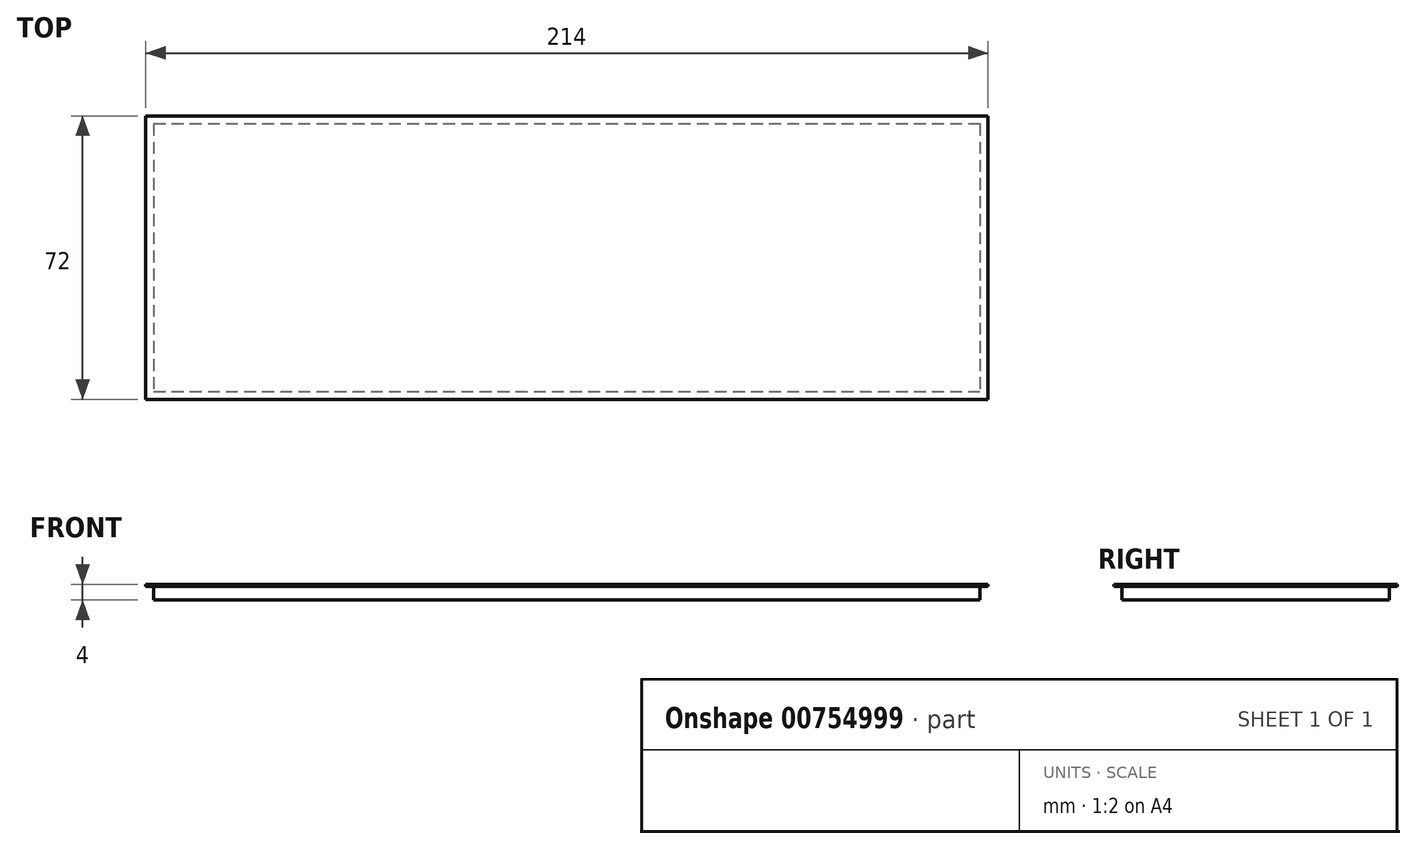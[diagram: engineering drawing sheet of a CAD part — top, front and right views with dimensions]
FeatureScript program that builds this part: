
annotation { "Feature Type Name" : "Feature", "Feature Type Description" : "" }
export const myFeature = defineFeature(function(context is Context, id is Id, definition is map)
    precondition{}
    {
        {
            var Q0;
            Q0=qCreatedBy(makeId("Top.planeOp"),FACE);
            var sketch = newSketch(context, id + "F0", { "sketchPlane" : qUnion([Q0])});
            skLineSegment(sketch, "E0.bottom", {"start": v(-72.86, 39.45) * mm, "end": v(137.14, 39.45) * mm});
            skLineSegment(sketch, "E0.top", {"start": v(-72.86, -28.55) * mm, "end": v(137.14, -28.55) * mm});
            skLineSegment(sketch, "E0.left", {"start": v(-72.86, 39.45) * mm, "end": v(-72.86, -28.55) * mm});
            skLineSegment(sketch, "E0.right", {"start": v(137.14, 39.45) * mm, "end": v(137.14, -28.55) * mm});
            skSolve(sketch);
        }
        {
            var Q0;
            Q0 = qSketchRegion(id + "F0", true);
            extrude(context, id + "F1", {"entities" : qUnion([Q0]), "depth" : 3.5 * mm, "offsetDistance" : 25 * mm});
        }
        {
            var Q0;
            Q0=makeQuery(id+"F1.opExtrude","CAP_FACE",FACE,{"disambiguationData":[OSD([sQuery(id+"F0.wireOp",EDGE,"E0.bottom"),sQuery(id+"F0.wireOp",EDGE,"E0.top"),sQuery(id+"F0.wireOp",EDGE,"E0.left"),sQuery(id+"F0.wireOp",EDGE,"E0.right")])],"isStart":false});
            var sketch = newSketch(context, id + "F2", { "sketchPlane" : qUnion([Q0])});
            skLineSegment(sketch, "E1.0", {"start": v(-74.86, 41.45) * mm, "end": v(-74.86, -30.55) * mm});
            skLineSegment(sketch, "E1.1", {"start": v(139.14, 41.45) * mm, "end": v(-74.86, 41.45) * mm});
            skLineSegment(sketch, "E1.2", {"start": v(139.14, -30.55) * mm, "end": v(139.14, 41.45) * mm});
            skLineSegment(sketch, "E1.3", {"start": v(-74.86, -30.55) * mm, "end": v(139.14, -30.55) * mm});
            skSolve(sketch);
        }
        {
            var Q0;
            Q0 = qSketchRegion(id + "F2", true);
            extrude(context, id + "F3", {"entities" : qUnion([Q0]), "operationType" : NewBodyOperationType.ADD, "depth" : 0.5 * mm, "offsetDistance" : 25 * mm});
        }
    });
